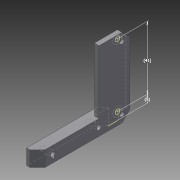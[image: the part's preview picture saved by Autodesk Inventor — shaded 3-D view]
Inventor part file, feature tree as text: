
AUTODESK INVENTOR PART (.ipt)
format: ipt  version: 2015 (Build 190159000, 159)  size: 141,312 bytes
history: native  units: mm
features: sketch x7, extrude x3, chamfer x3, hole x2
ambient origin geometry x8: Origin, YZ Plane, XZ Plane, XY Plane, X Axis, Y Axis, Z Axis, Center Point
bodies: Solid1 (feature_tree)
feature tree (15):
  extrude  "Extrusion1"  Depth=7.0mm
  hole  "Hole1"  [1 undecoded]
  chamfer  "Chamfer1"  Distance=5.0mm Angle=45.0deg
  extrude  "Extrusion2"  Depth=10.0mm
  extrude  "Extrusion3"  Depth=10.0mm
  hole  "Hole2"  [1 undecoded]
  chamfer  "Chamfer2"  Distance=15.0mm
  chamfer  "Chamfer3"  Distance=4.0mm
  sketch  "Sketch6"  dims[d8=3.0mm d9=6.0mm d10=4.0mm d11=2.0mm d12=90.0deg d13=7.0mm d14=20.594885mm d15=5.0mm d16=2.0mm d17=45.0deg]
  sketch  "Sketch7"  dims[d18=51.0mm d19=10.0mm d20=10.0mm d21=7.0mm d22=0.0mm d23=15.0mm d24=4.0mm d25=0.0mm d26=5.0mm d27=5.0mm d28=5.0mm d29=5.0mm d30=3.0mm d31=6.0mm d32=6.0mm d33=2.0mm d34=90.0deg d35=7.0mm d36=20.594885mm d37=5.0mm d38=2.0mm d39=45.0deg d40=4.0mm d41=2.0mm d42=45.0deg d43=41.0mm d44=5.0mm]
  sketch  "Sketch1"  dims[d0=7.0mm d1=50.0mm]
  sketch  "Sketch2"  dims[d2=10.0mm d3=0.0mm d4=10.0mm]
  sketch  "Sketch3"  dims[d5=5.0mm]
  sketch  "Sketch4"  dims[d6=5.0mm]
  sketch  "Sketch5"  dims[d7=30.0mm]
note: 2 required parameter values undecoded (feature->parameter linkage not recoverable at this tier; creation-order binding heuristic only, values carry confidence <= 0.55)
